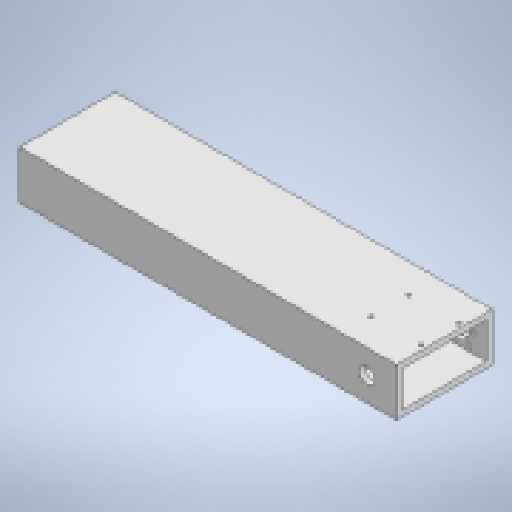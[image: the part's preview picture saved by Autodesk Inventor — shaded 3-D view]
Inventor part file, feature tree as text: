
AUTODESK INVENTOR PART (.ipt)
format: ipt  version: 2023 (Build 270158000, 158)  size: 178,688 bytes
history: native  units: in
note: dims shown in document units (in); Inventor stores cm internally (conversion verified against a paired STEP export)
features: extrude x5, sketch x5, shell x1
ambient origin geometry x8: Origin, YZ Plane, XZ Plane, XY Plane, X Axis, Y Axis, Z Axis, Center Point
bodies: Solid1 (feature_tree)
feature tree (11):
  extrude  "Extrusion1"  Depth=2.0in
  shell  "Shell1"  Thickness=15.748in
  extrude  "Extrusion2"  Depth=0.25in
  extrude  "Extrusion3"  Depth=1.5748in
  extrude  "Extrusion4"  Depth=11.811in TaperAngle=0.0deg
  extrude  "Extrusion5"  Depth=0.3937in
  sketch  "Sketch1"  dims[d0=4.0in d1=2.0in d2=15.748in d3=0.0in]
  sketch  "Sketch2"  dims[d4=0.25in d5=0.1575in]
  sketch  "Sketch3"  dims[d6=2.4803in d7=1.5748in]
  sketch  "Sketch4"  dims[d8=2.0866in d9=11.811in d10=0.0in]
  sketch  "Sketch5"  dims[d11=1.4961in d12=0.1575in d13=45.0deg d14=1.1024in d15=0.3937in d16=0.0in d17=0.6496in d18=0.3937in d19=0.0in d20=0.3937in d22=0.3937in d23=0.0in]
